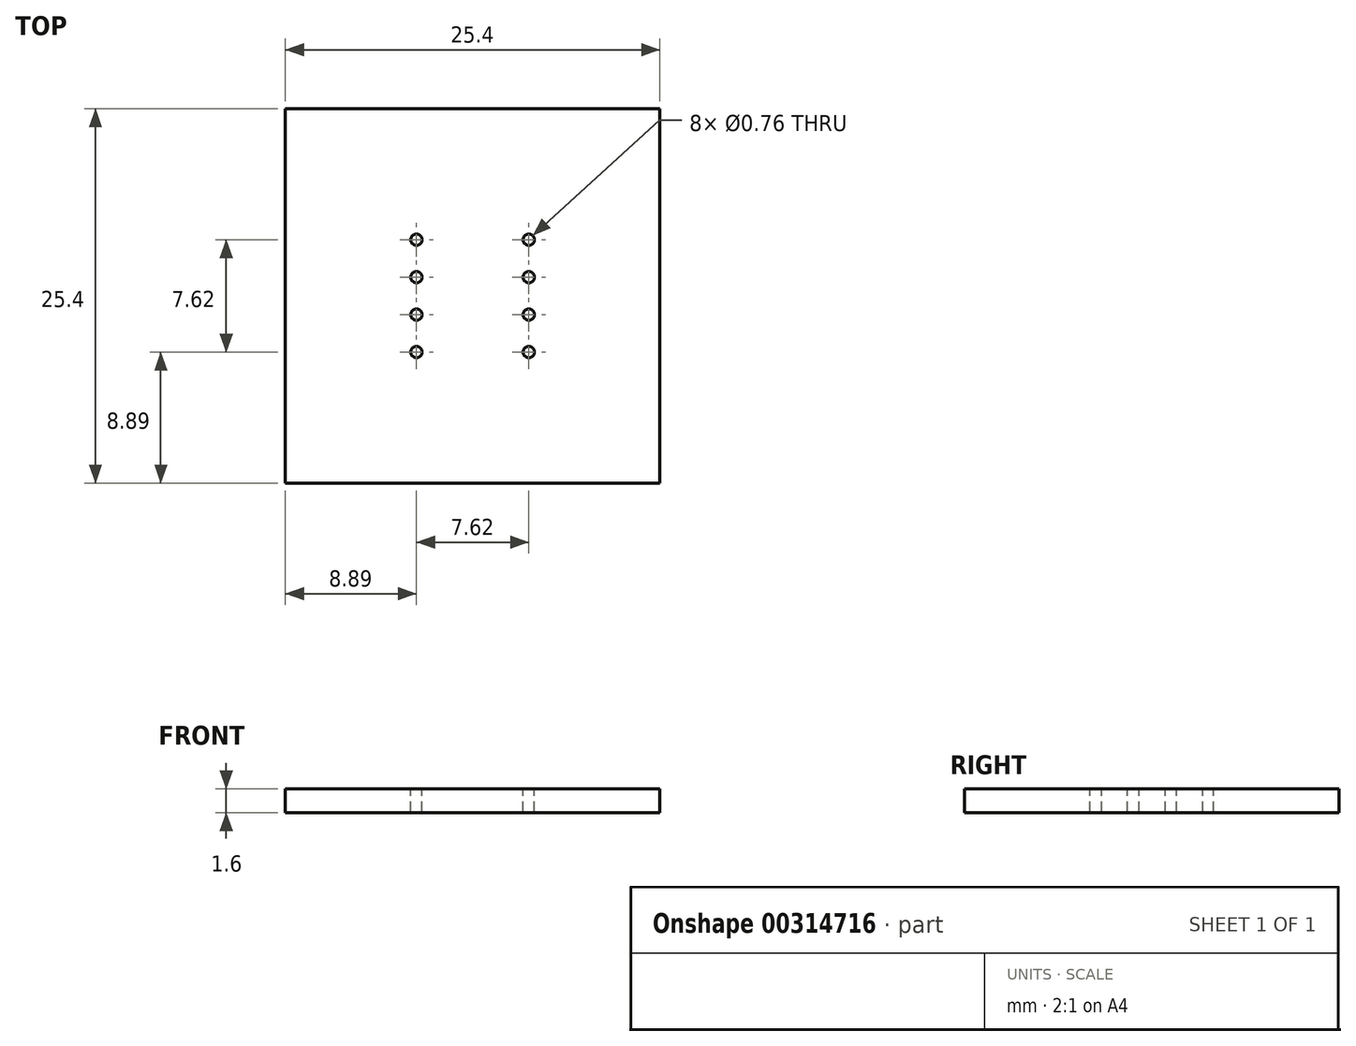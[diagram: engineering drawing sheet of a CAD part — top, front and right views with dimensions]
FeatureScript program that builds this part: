
annotation { "Feature Type Name" : "Feature", "Feature Type Description" : "" }
export const myFeature = defineFeature(function(context is Context, id is Id, definition is map)
    precondition{}
    {
        {
            var Q0;
            Q0=qCreatedBy(makeId("Top.planeOp"),FACE);
            var sketch = newSketch(context, id + "F0", { "sketchPlane" : qUnion([Q0])});
            skLineSegment(sketch, "E0.bottom", {"start": v(-12.7, 12.7) * mm, "end": v(12.7, 12.7) * mm});
            skLineSegment(sketch, "E0.top", {"start": v(-12.7, -12.7) * mm, "end": v(12.7, -12.7) * mm});
            skLineSegment(sketch, "E0.left", {"start": v(-12.7, 12.7) * mm, "end": v(-12.7, -12.7) * mm});
            skLineSegment(sketch, "E0.right", {"start": v(12.7, 12.7) * mm, "end": v(12.7, -12.7) * mm});
            skLineSegment(sketch, "E1", {"start": v(-12.7, -12.7) * mm, "end": v(12.7, 12.7) * mm, "construction": true});
            skSolve(sketch);
        }
        {
            var Q0;
            Q0=qSketchRegion(id+"F0",true);
            extrude(context, id + "F1", {"entities" : qUnion([Q0]), "oppositeDirection" : true, "depth" : 1.6 * mm});
        }
        {
            var Q0;
            Q0=makeQuery(id+"F1.opExtrude","CAP_FACE",FACE,{"disambiguationData":[OSD([sQuery(id+"F0.wireOp",EDGE,"E0.bottom"),sQuery(id+"F0.wireOp",EDGE,"E0.top"),sQuery(id+"F0.wireOp",EDGE,"E0.left"),sQuery(id+"F0.wireOp",EDGE,"E0.right")])],"isStart":true});
            var sketch = newSketch(context, id + "F2", { "sketchPlane" : qUnion([Q0])});
            skPoint(sketch, "E2", {"position": v(-3.81, 3.8) * mm});
            skPoint(sketch, "E3.0.1.0", {"position": v(-3.81, 1.27) * mm});
            skPoint(sketch, "E3.0.2.0", {"position": v(-3.81, -1.27) * mm});
            skPoint(sketch, "E3.0.3.0", {"position": v(-3.8, -3.81) * mm});
            skPoint(sketch, "E3.1.0.0", {"position": v(3.81, 3.81) * mm});
            skPoint(sketch, "E3.1.1.0", {"position": v(3.81, 1.27) * mm});
            skPoint(sketch, "E3.1.2.0", {"position": v(3.81, -1.27) * mm});
            skPoint(sketch, "E3.1.3.0", {"position": v(3.81, -3.81) * mm});
            skLineSegment(sketch, "E3.direction1", {"start": v(-3.81, 3.81) * mm, "end": v(3.81, 3.81) * mm, "construction": true});
            skLineSegment(sketch, "E3.direction2", {"start": v(-3.81, 3.8) * mm, "end": v(-3.81, 1.27) * mm, "construction": true});
            skLineSegment(sketch, "E4", {"start": v(3.81, 3.81) * mm, "end": v(-3.81, -3.81) * mm, "construction": true});
            skSolve(sketch);
        }
        {
            var Q0;
            Q0=sQuery(id+"F2.wireOp",VERTEX,"E2");
            var Q1;
            Q1=sQuery(id+"F2.wireOp",VERTEX,"E3.0.1.0");
            var Q2;
            Q2=sQuery(id+"F2.wireOp",VERTEX,"E3.0.2.0");
            var Q3;
            Q3=sQuery(id+"F2.wireOp",VERTEX,"E3.0.3.0");
            var Q4;
            Q4=sQuery(id+"F2.wireOp",VERTEX,"E3.1.2.0");
            var Q5;
            Q5=sQuery(id+"F2.wireOp",VERTEX,"E3.1.1.0");
            var Q6;
            Q6=sQuery(id+"F2.wireOp",VERTEX,"E3.1.0.0");
            var Q7;
            Q7=sQuery(id+"F2.wireOp",VERTEX,"E3.1.3.0");
            var Q8;
            Q8=makeQuery(id+"F1.opExtrude","SWEPT_BODY",BODY,{"disambiguationData":[OSD([sQuery(id+"F0.wireOp",EDGE,"E0.bottom"),sQuery(id+"F0.wireOp",EDGE,"E0.top"),sQuery(id+"F0.wireOp",EDGE,"E0.left"),sQuery(id+"F0.wireOp",EDGE,"E0.right")])]});
            hole(context, id + "F3", {"style" : HoleStyle.SIMPLE, "endStyle" : HoleEndStyle.THROUGH, "holeDiameter" : 0.76 * mm, "locations" : qUnion([Q0, Q1, Q2, Q3, Q4, Q5, Q6, Q7]), "scope" : qUnion([Q8]), "isTappedThrough" : true});
        }
    });
